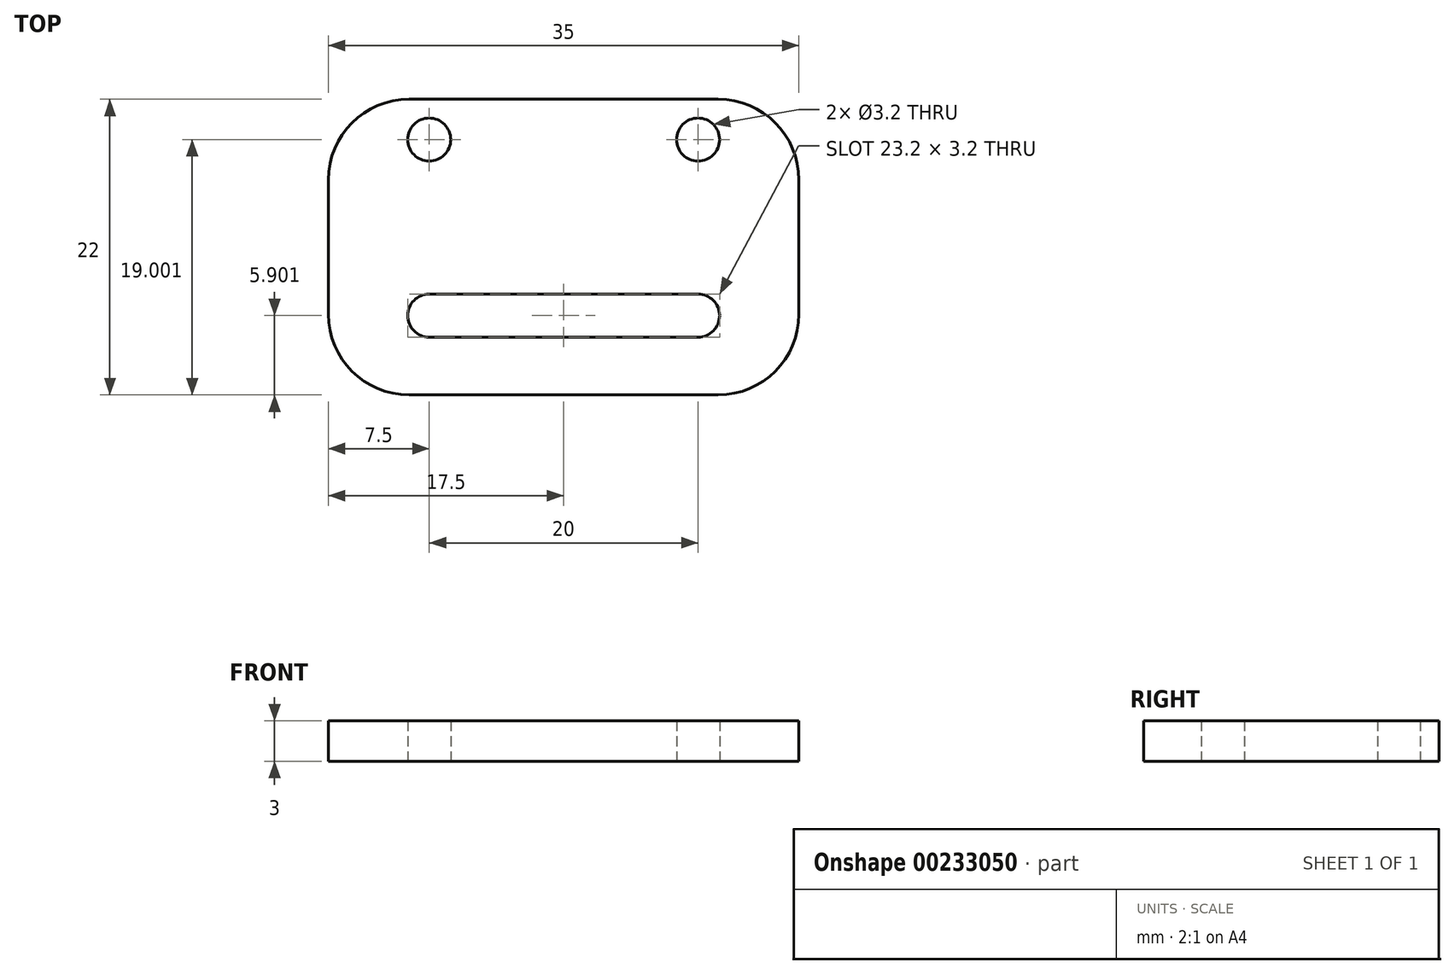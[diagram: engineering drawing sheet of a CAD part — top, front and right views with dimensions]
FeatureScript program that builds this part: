
annotation { "Feature Type Name" : "Feature", "Feature Type Description" : "" }
export const myFeature = defineFeature(function(context is Context, id is Id, definition is map)
    precondition{}
    {
        {
            var Q0;
            Q0=qCreatedBy(makeId("Top.planeOp"),FACE);
            var sketch = newSketch(context, id + "F0", { "sketchPlane" : qUnion([Q0])});
            skLineSegment(sketch, "E0.bottom", {"start": v(-17.5, 12.53) * mm, "end": v(17.5, 12.53) * mm});
            skLineSegment(sketch, "E0.top", {"start": v(-17.5, -9.47) * mm, "end": v(17.5, -9.47) * mm});
            skLineSegment(sketch, "E0.left", {"start": v(-17.5, 12.53) * mm, "end": v(-17.5, -9.47) * mm});
            skLineSegment(sketch, "E0.right", {"start": v(17.5, 12.53) * mm, "end": v(17.5, -9.47) * mm});
            skCircle(sketch, "E1", {"center": v(-10, 9.53) * mm, "radius": 1.6 * mm});
            skCircle(sketch, "E2", {"center": v(10, 9.53) * mm, "radius": 1.6 * mm});
            skLineSegment(sketch, "E3", {"start": v(-10, -1.97) * mm, "end": v(10, -1.97) * mm});
            skArc(sketch, "E4", {"start": v(10, -5.17) * mm, "mid": v(11.6, -3.57) * mm, "end": v(10, -1.97) * mm});
            skLineSegment(sketch, "E5", {"start": v(10, -5.17) * mm, "end": v(-10, -5.17) * mm});
            skArc(sketch, "E6", {"start": v(-10, -1.97) * mm, "mid": v(-11.6, -3.57) * mm, "end": v(-10, -5.17) * mm});
            skSolve(sketch);
        }
        {
            var Q0;
            Q0=makeQuery(id+"F0.imprint","IMPRINT",FACE,{"disambiguationData":[TD([[makeQuery(id+"F0.imprint","IMPRINT",EDGE,{"derivedFrom":sQuery(id+"F0.wireOp",EDGE,"E0.bottom")}),-1.0]])]});
            extrude(context, id + "F1", {"entities" : qUnion([Q0]), "depth" : 3 * mm});
        }
        {
            var Q0;
            Q0=makeQuery(id+"F1.opExtrude","SWEPT_EDGE",EDGE,{"disambiguationData":[OSD([sQuery(id+"F0.wireOp",EDGE,"E0.top"),sQuery(id+"F0.wireOp",EDGE,"E0.left")])]});
            var Q1;
            Q1=makeQuery(id+"F1.opExtrude","SWEPT_EDGE",EDGE,{"disambiguationData":[OSD([sQuery(id+"F0.wireOp",EDGE,"E0.bottom"),sQuery(id+"F0.wireOp",EDGE,"E0.left")])]});
            var Q2;
            Q2=makeQuery(id+"F1.opExtrude","SWEPT_EDGE",EDGE,{"disambiguationData":[OSD([sQuery(id+"F0.wireOp",EDGE,"E0.bottom"),sQuery(id+"F0.wireOp",EDGE,"E0.right")])]});
            var Q3;
            Q3=makeQuery(id+"F1.opExtrude","SWEPT_EDGE",EDGE,{"disambiguationData":[OSD([sQuery(id+"F0.wireOp",EDGE,"E0.top"),sQuery(id+"F0.wireOp",EDGE,"E0.right")])]});
            fillet(context, id + "F2", {"entities" : qUnion([Q0, Q1, Q2, Q3]), "radius" : 6 * mm, "tangentPropagation" : true, "allowEdgeOverflow" : false});
        }
    });
